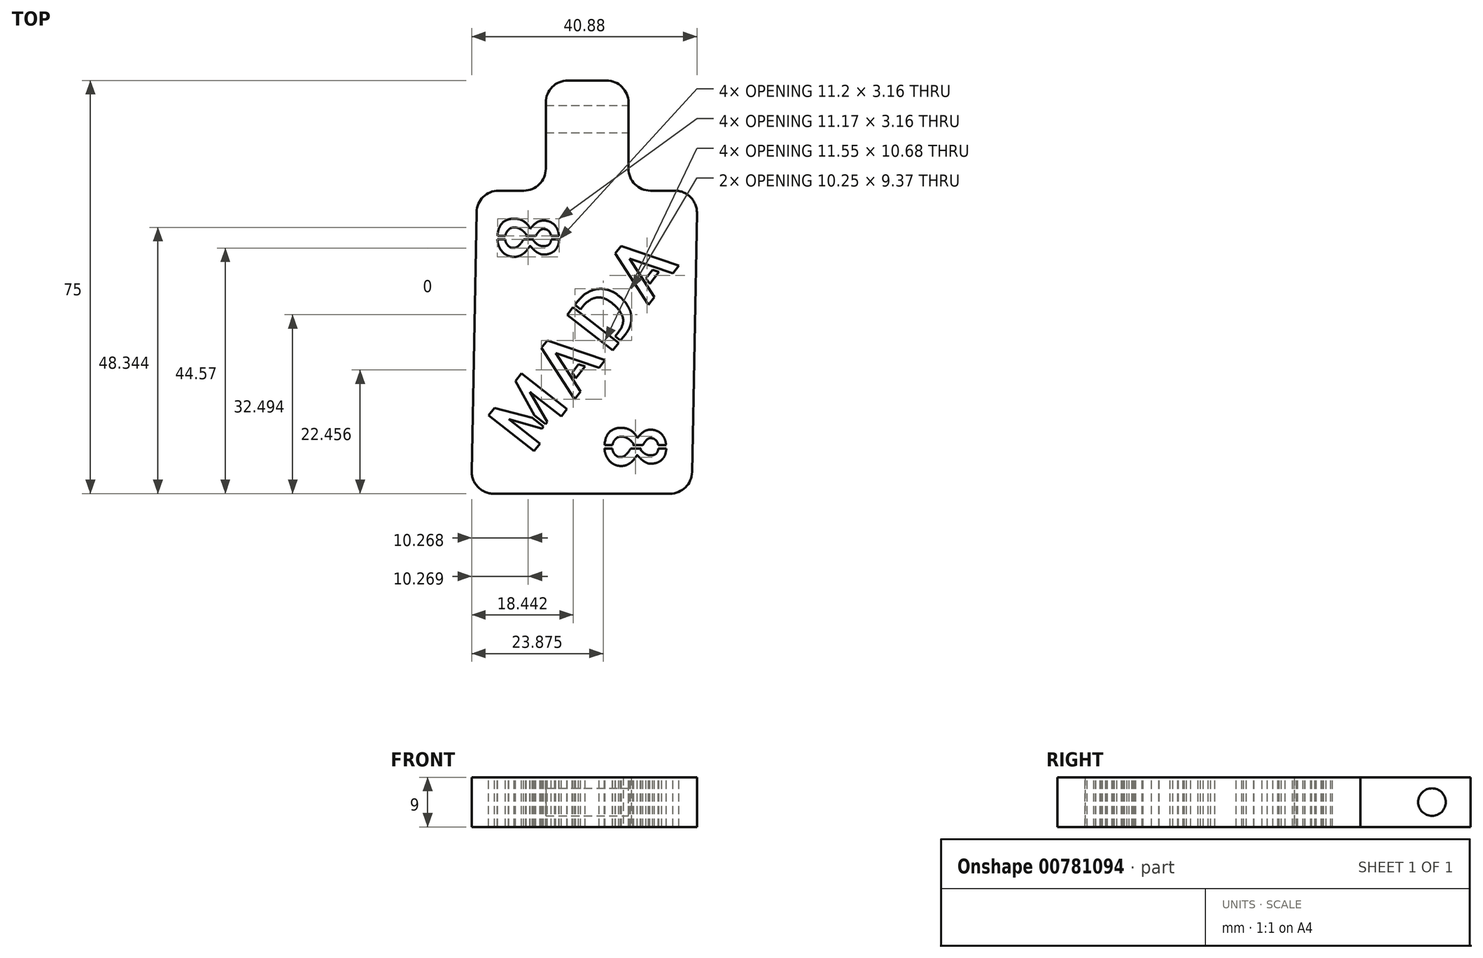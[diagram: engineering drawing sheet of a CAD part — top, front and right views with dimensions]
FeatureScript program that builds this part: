
annotation { "Feature Type Name" : "Feature", "Feature Type Description" : "" }
export const myFeature = defineFeature(function(context is Context, id is Id, definition is map)
    precondition{}
    {
        {
            var Q0;
            Q0=qCreatedBy(makeId("Top.planeOp"),FACE);
            var sketch = newSketch(context, id + "F0", { "sketchPlane" : qUnion([Q0])});
            skLineSegment(sketch, "E0.bottom", {"start": v(20.51, 27.5) * mm, "end": v(-19.49, 27.5) * mm});
            skLineSegment(sketch, "E0.top", {"start": v(19.49, -27.5) * mm, "end": v(-20.51, -27.5) * mm});
            skLineSegment(sketch, "E0.right", {"start": v(-19.49, 27.5) * mm, "end": v(-20.51, -27.5) * mm});
            skPoint(sketch, "E0.middle", {"position": v(0, 0) * mm});
            skLineSegment(sketch, "E1.bottom", {"start": v(8.01, 47.5) * mm, "end": v(-6.99, 47.5) * mm});
            skLineSegment(sketch, "E1.top", {"start": v(8.01, 27.5) * mm, "end": v(-6.99, 27.5) * mm});
            skLineSegment(sketch, "E1.left", {"start": v(8.01, 47.5) * mm, "end": v(8.01, 27.5) * mm});
            skLineSegment(sketch, "E1.right", {"start": v(-6.99, 47.5) * mm, "end": v(-6.99, 27.5) * mm});
            skPoint(sketch, "E1.middle", {"position": v(0.51, 37.5) * mm});
            skPoint(sketch, "E1.middle.positionSnap0", {"position": v(0.51, 27.5) * mm});
            skPoint(sketch, "E1.centerSnap0", {"position": v(0.51, 27.5) * mm});
            skText(sketch, "E2", { "text": "MADA", "fontName": "AllertaStencil-Regular.ttf"});
            skText(sketch, "E3", { "text": "8", "fontName": "AllertaStencil-Regular.ttf"});
            skText(sketch, "E4", { "text": "8", "fontName": "AllertaStencil-Regular.ttf"});
            skLineSegment(sketch, "E5", {"start": v(19.49, -27.5) * mm, "end": v(20.51, 27.5) * mm});
            const initialGuessF0  = {"E2": [-0.00991, -0.0208, 0.61566, 0.78801, 0.0105], "E3": [-0.01564, 0.0235, 0, -1, 0.011], "E4": [0.0038, -0.01447, 0, -1, 0.011]};
            skSetInitialGuess(sketch, initialGuessF0);
            skSolve(sketch);
        }
        {
            var Q0;
            Q0 = qSketchRegion(id + "F0", true);
            var Q1;
            Q1 = qConstructionFilter(qBodyType(qCreatedBy(id + "F0" ,EDGE), BodyType.WIRE), ConstructionObject.NO);
            extrude(context, id + "F1", {"entities" : qUnion([Q0]), "surfaceEntities" : qUnion([Q1]), "oppositeDirection" : true, "depth" : 9 * mm, "offsetDistance" : 25 * mm});
        }
        {
            var Q0;
            Q0=makeQuery(id+"F1.opExtrude","SWEPT_FACE",FACE,{"disambiguationData":[OSD([sQuery(id+"F0.wireOp",EDGE,"E1.left")])]});
            var sketch = newSketch(context, id + "F2", { "sketchPlane" : qUnion([Q0])});
            skCircle(sketch, "E6", {"center": v(40.5, -4.5) * mm, "radius": 2.5 * mm});
            skPoint(sketch, "E6.centerSnap0", {"position": v(47.5, -4.5) * mm});
            skSolve(sketch);
        }
        {
            var Q0;
            Q0=makeQuery(id+"F2.imprint","IMPRINT",FACE,{"disambiguationData":[TD([[makeQuery(id+"F2.imprint","IMPRINT",EDGE,{"derivedFrom":sQuery(id+"F2.wireOp",EDGE,"E6")}),1.0]])]});
            extrude(context, id + "F3", {"entities" : qUnion([Q0]), "operationType" : NewBodyOperationType.REMOVE, "oppositeDirection" : true, "depth" : 25 * mm, "offsetDistance" : 25 * mm});
        }
        {
            var Q0;
            Q0=makeQuery(id+"F1.opExtrude","SWEPT_EDGE",EDGE,{"disambiguationData":[OSD([sQuery(id+"F0.wireOp",EDGE,"E0.top"),sQuery(id+"F0.wireOp",EDGE,"E0.left")])]});
            var Q1;
            Q1=makeQuery(id+"F1.opExtrude","SWEPT_EDGE",EDGE,{"disambiguationData":[OSD([sQuery(id+"F0.wireOp",EDGE,"E0.bottom"),sQuery(id+"F0.wireOp",EDGE,"E0.left")])]});
            var Q2;
            Q2=makeQuery(id+"F1.opExtrude","SWEPT_EDGE",EDGE,{"disambiguationData":[OSD([sQuery(id+"F0.wireOp",EDGE,"E0.top"),sQuery(id+"F0.wireOp",EDGE,"E0.right")])]});
            var Q3;
            Q3=makeQuery(id+"F1.opExtrude","SWEPT_EDGE",EDGE,{"disambiguationData":[OSD([sQuery(id+"F0.wireOp",EDGE,"E0.bottom"),sQuery(id+"F0.wireOp",EDGE,"E0.right")])]});
            var Q4;
            Q4=makeQuery(id+"F1.opExtrude","SWEPT_EDGE",EDGE,{"disambiguationData":[OSD([sQuery(id+"F0.wireOp",EDGE,"E1.bottom"),sQuery(id+"F0.wireOp",EDGE,"E1.right")])]});
            var Q5;
            Q5=makeQuery(id+"F1.opExtrude","SWEPT_EDGE",EDGE,{"disambiguationData":[OSD([sQuery(id+"F0.wireOp",EDGE,"E1.bottom"),sQuery(id+"F0.wireOp",EDGE,"E1.left")])]});
            var Q6;
            Q6=makeQuery(id+"F1.opExtrude","SWEPT_EDGE",EDGE,{"disambiguationData":[OSD([sQuery(id+"F0.wireOp",EDGE,"E0.bottom"),sQuery(id+"F0.wireOp",EDGE,"E1.top"),sQuery(id+"F0.wireOp",EDGE,"E1.right")])]});
            var Q7;
            Q7=makeQuery(id+"F1.opExtrude","SWEPT_EDGE",EDGE,{"disambiguationData":[OSD([sQuery(id+"F0.wireOp",EDGE,"E0.bottom"),sQuery(id+"F0.wireOp",EDGE,"E1.top"),sQuery(id+"F0.wireOp",EDGE,"E1.left")])]});
            fillet(context, id + "F4", {"entities" : qUnion([Q0, Q1, Q2, Q3, Q4, Q5, Q6, Q7]), "radius" : 4 * mm, "tangentPropagation" : true, "allowEdgeOverflow" : false});
        }
    });
